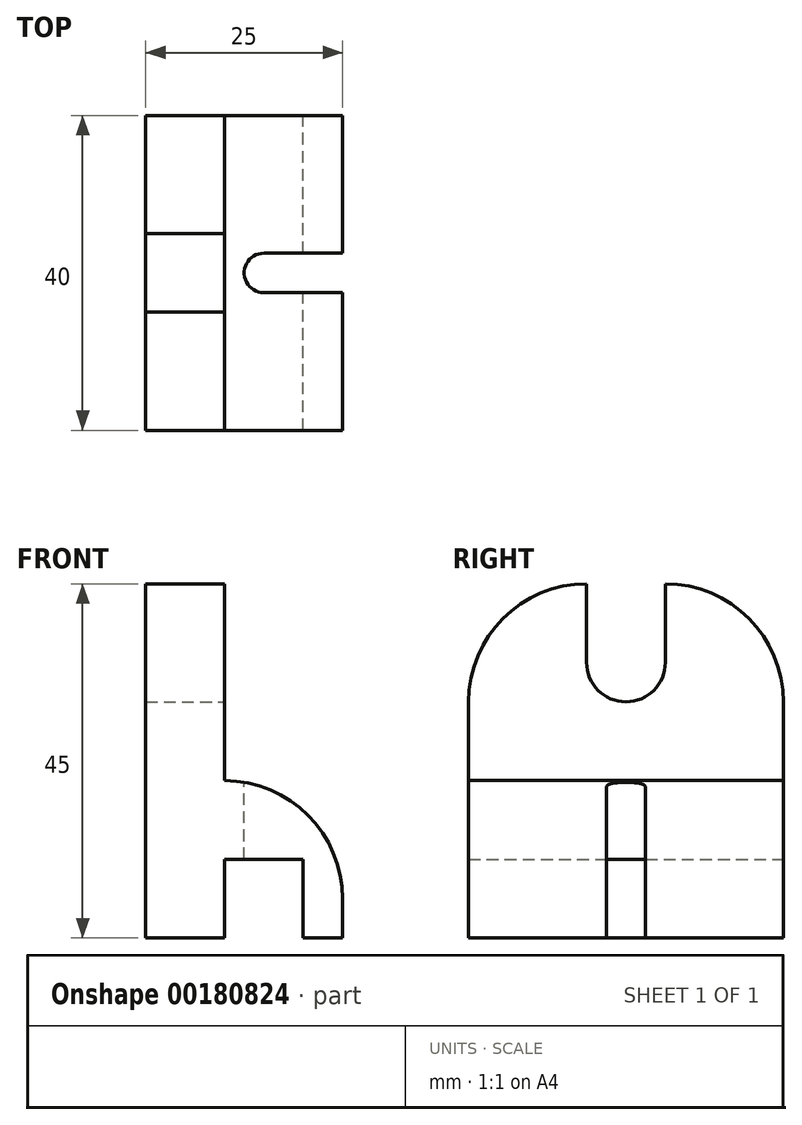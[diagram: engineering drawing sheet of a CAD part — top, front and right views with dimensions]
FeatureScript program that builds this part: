
annotation { "Feature Type Name" : "Feature", "Feature Type Description" : "" }
export const myFeature = defineFeature(function(context is Context, id is Id, definition is map)
    precondition{}
    {
        {
            var Q0;
            Q0=qCreatedBy(makeId("Right.planeOp"),FACE);
            var sketch = newSketch(context, id + "F0", { "sketchPlane" : qUnion([Q0])});
            skLineSegment(sketch, "E0.bottom", {"start": v(0, 0) * mm, "end": v(40, 0) * mm});
            skLineSegment(sketch, "E0.top", {"start": v(0, 20) * mm, "end": v(40, 20) * mm});
            skLineSegment(sketch, "E0.left", {"start": v(0, 0) * mm, "end": v(0, 20) * mm});
            skLineSegment(sketch, "E0.right", {"start": v(40, 0) * mm, "end": v(40, 20) * mm});
            skSolve(sketch);
        }
        {
            var Q0;
            Q0=makeQuery(id+"F0.imprint","IMPRINT",FACE,{"disambiguationData":[TD([[makeQuery(id+"F0.imprint","IMPRINT",EDGE,{"derivedFrom":sQuery(id+"F0.wireOp",EDGE,"E0.bottom")}),1.0]])]});
            extrude(context, id + "F1", {"entities" : qUnion([Q0]), "depth" : 25 * mm});
        }
        {
            var Q0;
            Q0=makeQuery(id+"F1.opExtrude","SWEPT_FACE",FACE,{"disambiguationData":[OSD([sQuery(id+"F0.wireOp",EDGE,"E0.top")])]});
            var sketch = newSketch(context, id + "F2", { "sketchPlane" : qUnion([Q0])});
            skLineSegment(sketch, "E1", {"start": v(0, 0) * mm, "end": v(10, 0) * mm});
            skLineSegment(sketch, "E2", {"start": v(10, 0) * mm, "end": v(10, 40) * mm});
            skLineSegment(sketch, "E3", {"start": v(10, 40) * mm, "end": v(0, 40) * mm});
            skLineSegment(sketch, "E4", {"start": v(0, 40) * mm, "end": v(0, 0) * mm});
            skSolve(sketch);
        }
        {
            var Q0;
            Q0=makeQuery(id+"F2.imprint","IMPRINT",FACE,{"disambiguationData":[TD([[makeQuery(id+"F2.imprint","IMPRINT",EDGE,{"derivedFrom":sQuery(id+"F2.wireOp",EDGE,"E1")}),-1.0]])]});
            extrude(context, id + "F3", {"entities" : qUnion([Q0]), "operationType" : NewBodyOperationType.ADD, "depth" : 25 * mm});
        }
        {
            var Q0;
            Q0=makeQuery(id+"F3.opExtrude","SWEPT_FACE",FACE,{"disambiguationData":[OSD([sQuery(id+"F2.wireOp",EDGE,"E2")])]});
            var sketch = newSketch(context, id + "F4", { "sketchPlane" : qUnion([Q0])});
            skLineSegment(sketch, "E5", {"start": v(20, 45) * mm, "end": v(20, 35) * mm, "construction": true});
            skArc(sketch, "E6", {"start": v(15, 35) * mm, "mid": v(20, 30) * mm, "end": v(25, 35) * mm});
            skLineSegment(sketch, "E7", {"start": v(20, 35) * mm, "end": v(15, 35) * mm, "construction": true});
            skLineSegment(sketch, "E8", {"start": v(20, 35) * mm, "end": v(25, 35) * mm, "construction": true});
            skLineSegment(sketch, "E9", {"start": v(15, 35) * mm, "end": v(15, 47.68) * mm});
            skLineSegment(sketch, "E10", {"start": v(15, 47.68) * mm, "end": v(25, 47.68) * mm});
            skLineSegment(sketch, "E11", {"start": v(25, 47.68) * mm, "end": v(25, 35) * mm});
            skSolve(sketch);
        }
        {
            var Q0;
            {var subQ0=sQuery(id+"F4.wireOp",EDGE,"E6");Q0=makeQuery(id+"F4.imprint","IMPRINT",FACE,{"disambiguationData":[TD([[makeQuery(id+"F4.imprint","IMPRINT",EDGE,{"derivedFrom":subQ0}),1.0]])]});}
            var Q1;
            {var subQ0=sQuery(id+"F4.wireOp",EDGE,"E10");Q1=makeQuery(id+"F4.imprint","IMPRINT",FACE,{"disambiguationData":[TD([[makeQuery(id+"F4.imprint","IMPRINT",EDGE,{"derivedFrom":subQ0}),-1.0]])]});}
            extrude(context, id + "F5", {"entities" : qUnion([Q0, Q1]), "operationType" : NewBodyOperationType.REMOVE, "oppositeDirection" : true, "depth" : 50 * mm});
        }
        {
            var Q0;
            Q0=makeQuery(id+"F1.opExtrude","SWEPT_FACE",FACE,{"disambiguationData":[OSD([sQuery(id+"F0.wireOp",EDGE,"E0.top")])]});
            var sketch = newSketch(context, id + "F6", { "sketchPlane" : qUnion([Q0])});
            skLineSegment(sketch, "E12", {"start": v(25, 20) * mm, "end": v(15, 20) * mm, "construction": true});
            skArc(sketch, "E13", {"start": v(15, 22.5) * mm, "mid": v(12.5, 20) * mm, "end": v(15, 17.5) * mm});
            skLineSegment(sketch, "E14", {"start": v(15, 20) * mm, "end": v(15, 17.5) * mm, "construction": true});
            skLineSegment(sketch, "E15", {"start": v(15, 20) * mm, "end": v(15, 22.5) * mm, "construction": true});
            skLineSegment(sketch, "E16", {"start": v(15, 17.5) * mm, "end": v(25, 17.5) * mm});
            skLineSegment(sketch, "E17", {"start": v(15, 22.5) * mm, "end": v(25, 22.5) * mm});
            skSolve(sketch);
        }
        {
            var Q0;
            Q0=makeQuery(id+"F6.imprint","IMPRINT",FACE,{"disambiguationData":[TD([[makeQuery(id+"F6.imprint","IMPRINT",EDGE,{"derivedFrom":sQuery(id+"F6.wireOp",EDGE,"E13")}),1.0]])]});
            extrude(context, id + "F7", {"entities" : qUnion([Q0]), "operationType" : NewBodyOperationType.REMOVE, "oppositeDirection" : true, "depth" : 50 * mm});
        }
        {
            var Q0;
            Q0=makeQuery(id+"F3.opExtrude","CAP_EDGE",EDGE,{"disambiguationData":[OSD([sQuery(id+"F2.wireOp",EDGE,"E3")])],"isStart":false});
            var Q1;
            Q1=makeQuery(id+"F3.opExtrude","CAP_EDGE",EDGE,{"disambiguationData":[OSD([sQuery(id+"F2.wireOp",EDGE,"E1")])],"isStart":false});
            fillet(context, id + "F8", {"entities" : qUnion([Q0, Q1]), "radius" : 15 * mm, "tangentPropagation" : true, "allowEdgeOverflow" : false});
        }
        {
            var Q0;
            {var subQ0=sQuery(id+"F0.wireOp",EDGE,"E0.right");var subQ1=sQuery(id+"F0.wireOp",EDGE,"E0.top");Q0=makeQuery(id+"F7.boolean.opBoolean","SPLIT",EDGE,{"disambiguationData":[TD([makeQuery(id+"F1.opExtrude","SWEPT_FACE",FACE,{"disambiguationData":[OSD([subQ0])]})])],"derivedFrom":makeQuery(id+"F1.opExtrude","CAP_EDGE",EDGE,{"disambiguationData":[OSD([subQ1])],"isStart":false})});}
            var Q1;
            {var subQ0=sQuery(id+"F0.wireOp",EDGE,"E0.left");var subQ1=sQuery(id+"F0.wireOp",EDGE,"E0.top");Q1=makeQuery(id+"F7.boolean.opBoolean","SPLIT",EDGE,{"disambiguationData":[TD([makeQuery(id+"F1.opExtrude","SWEPT_FACE",FACE,{"disambiguationData":[OSD([subQ0])]})])],"derivedFrom":makeQuery(id+"F1.opExtrude","CAP_EDGE",EDGE,{"disambiguationData":[OSD([subQ1])],"isStart":false})});}
            fillet(context, id + "F9", {"entities" : qUnion([Q0, Q1]), "radius" : 15 * mm, "tangentPropagation" : true, "allowEdgeOverflow" : false});
        }
        {
            var Q0;
            Q0=makeQuery(id+"F3.boolean.opBoolean","MERGE",FACE,{"derivedFrom":[makeQuery(id+"F1.opExtrude","SWEPT_FACE",FACE,{"disambiguationData":[OSD([sQuery(id+"F0.wireOp",EDGE,"E0.right")])]}),makeQuery(id+"F3.opExtrude","SWEPT_FACE",FACE,{"disambiguationData":[OSD([sQuery(id+"F2.wireOp",EDGE,"E3")])]})]});
            var sketch = newSketch(context, id + "F10", { "sketchPlane" : qUnion([Q0])});
            skLineSegment(sketch, "E18", {"start": v(0, 0) * mm, "end": v(-10, 0) * mm, "construction": true});
            skLineSegment(sketch, "E19", {"start": v(-10, 0) * mm, "end": v(-10, 10) * mm});
            skLineSegment(sketch, "E20", {"start": v(-10, 10) * mm, "end": v(-20, 10) * mm});
            skLineSegment(sketch, "E21", {"start": v(-20, 10) * mm, "end": v(-20, 0) * mm});
            skLineSegment(sketch, "E22", {"start": v(-20, 0) * mm, "end": v(-10, 0) * mm});
            skSolve(sketch);
        }
        {
            var Q0;
            Q0=makeQuery(id+"F10.imprint","IMPRINT",FACE,{"disambiguationData":[TD([[makeQuery(id+"F10.imprint","IMPRINT",EDGE,{"derivedFrom":sQuery(id+"F10.wireOp",EDGE,"E19")}),1.0]])]});
            extrude(context, id + "F11", {"entities" : qUnion([Q0]), "operationType" : NewBodyOperationType.REMOVE, "oppositeDirection" : true, "depth" : 100 * mm});
        }
    });
